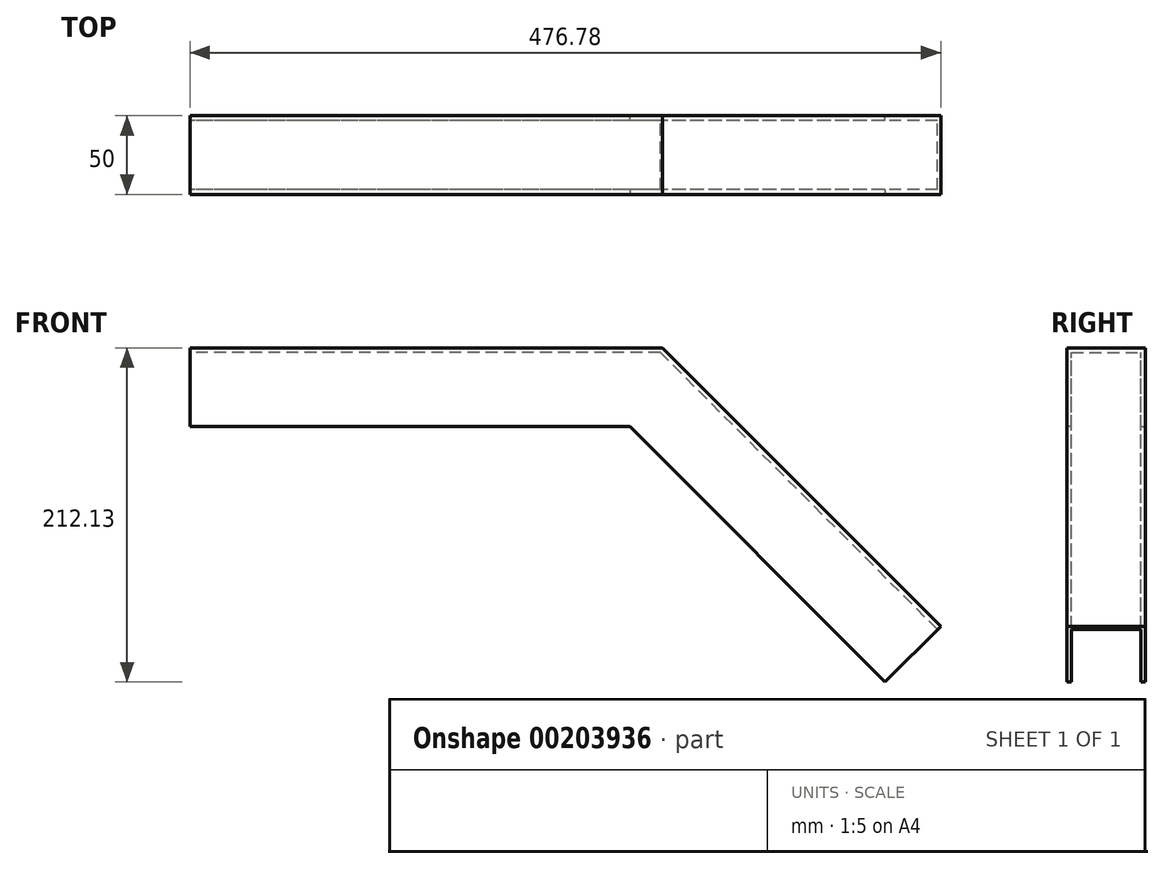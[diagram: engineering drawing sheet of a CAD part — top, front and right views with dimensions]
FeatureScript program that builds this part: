
annotation { "Feature Type Name" : "Feature", "Feature Type Description" : "" }
export const myFeature = defineFeature(function(context is Context, id is Id, definition is map)
    precondition{}
    {
        {
            var Q0;
            Q0=qCreatedBy(makeId("Front.planeOp"),FACE);
            var sketch = newSketch(context, id + "F0", { "sketchPlane" : qUnion([Q0])});
            skLineSegment(sketch, "E0", {"start": v(0, 0) * mm, "end": v(300, 0) * mm});
            skLineSegment(sketch, "E1", {"start": v(300, 0) * mm, "end": v(476.78, -176.78) * mm});
            skLineSegment(sketch, "E2", {"start": v(476.78, -176.78) * mm, "end": v(474.66, -178.9) * mm});
            skLineSegment(sketch, "E3", {"start": v(474.66, -178.9) * mm, "end": v(298.76, -3) * mm});
            skLineSegment(sketch, "E4", {"start": v(298.76, -3) * mm, "end": v(0, -3) * mm});
            skLineSegment(sketch, "E5", {"start": v(0, -3) * mm, "end": v(0, 0) * mm});
            skSolve(sketch);
        }
        {
            var Q0;
            Q0 = qSketchRegion(id + "F0", true);
            extrude(context, id + "F1", {"entities" : qUnion([Q0]), "depth" : 50 * mm});
        }
        {
            var Q0;
            Q0=makeQuery(id+"F1.opExtrude","CAP_FACE",FACE,{"disambiguationData":[OSD([sQuery(id+"F0.wireOp",EDGE,"E0"),sQuery(id+"F0.wireOp",EDGE,"E1"),sQuery(id+"F0.wireOp",EDGE,"E2"),sQuery(id+"F0.wireOp",EDGE,"E3"),sQuery(id+"F0.wireOp",EDGE,"E4"),sQuery(id+"F0.wireOp",EDGE,"E5")])],"isStart":false});
            var sketch = newSketch(context, id + "F2", { "sketchPlane" : qUnion([Q0])});
            skLineSegment(sketch, "E6", {"start": v(298.76, -3) * mm, "end": v(474.66, -178.9) * mm});
            skLineSegment(sketch, "E7", {"start": v(474.66, -178.9) * mm, "end": v(441.42, -212.13) * mm});
            skLineSegment(sketch, "E8", {"start": v(441.42, -212.13) * mm, "end": v(279.29, -50) * mm});
            skLineSegment(sketch, "E9", {"start": v(279.29, -50) * mm, "end": v(0, -50) * mm});
            skLineSegment(sketch, "E10", {"start": v(0, -50) * mm, "end": v(0, -3) * mm});
            skLineSegment(sketch, "E11", {"start": v(0, -3) * mm, "end": v(298.76, -3) * mm});
            skSolve(sketch);
        }
        {
            var Q0;
            Q0 = qSketchRegion(id + "F2", true);
            extrude(context, id + "F3", {"entities" : qUnion([Q0]), "operationType" : NewBodyOperationType.ADD, "oppositeDirection" : true, "depth" : 3 * mm});
        }
        {
            var Q0;
            Q0=makeQuery(id+"F1.opExtrude","CAP_FACE",FACE,{"disambiguationData":[OSD([sQuery(id+"F0.wireOp",EDGE,"E0"),sQuery(id+"F0.wireOp",EDGE,"E1"),sQuery(id+"F0.wireOp",EDGE,"E2"),sQuery(id+"F0.wireOp",EDGE,"E3"),sQuery(id+"F0.wireOp",EDGE,"E4"),sQuery(id+"F0.wireOp",EDGE,"E5")])],"isStart":true});
            var sketch = newSketch(context, id + "F4", { "sketchPlane" : qUnion([Q0])});
            skLineSegment(sketch, "E12", {"start": v(-474.66, -178.9) * mm, "end": v(-441.42, -212.13) * mm});
            skLineSegment(sketch, "E13", {"start": v(-441.42, -212.13) * mm, "end": v(-279.29, -50) * mm});
            skLineSegment(sketch, "E14", {"start": v(-279.29, -50) * mm, "end": v(0, -50) * mm});
            skLineSegment(sketch, "E15", {"start": v(0, -50) * mm, "end": v(0, -3) * mm});
            skLineSegment(sketch, "E16", {"start": v(0, -3) * mm, "end": v(-298.76, -3) * mm});
            skLineSegment(sketch, "E17", {"start": v(-298.76, -3) * mm, "end": v(-474.66, -178.9) * mm});
            skSolve(sketch);
        }
        {
            var Q0;
            Q0 = qSketchRegion(id + "F4", true);
            extrude(context, id + "F5", {"entities" : qUnion([Q0]), "operationType" : NewBodyOperationType.ADD, "oppositeDirection" : true, "depth" : 3 * mm});
        }
    });
